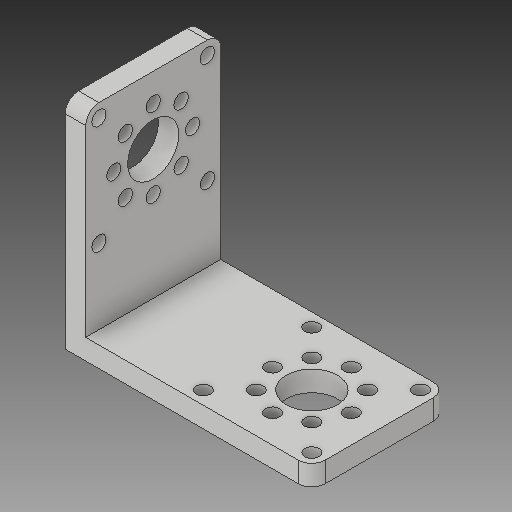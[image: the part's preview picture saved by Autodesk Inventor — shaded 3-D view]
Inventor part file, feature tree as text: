
AUTODESK INVENTOR PART (.ipt)
format: ipt  version: 2017 (Build 210142000, 142)  size: 185,856 bytes
history: native  units: in
note: dims shown in document units (in); Inventor stores cm internally (conversion verified against a paired STEP export)
features: fillet x1
ambient origin geometry x8: Origin, YZ Plane, XZ Plane, XY Plane, X Axis, Y Axis, Z Axis, Center Point
bodies: Solid1 (feature_tree)
feature tree (1):
  fillet  "Fillet1"  [1 undecoded]
note: 1 required parameter value undecoded (feature->parameter linkage not recoverable at this tier; creation-order binding heuristic only, values carry confidence <= 0.55)
